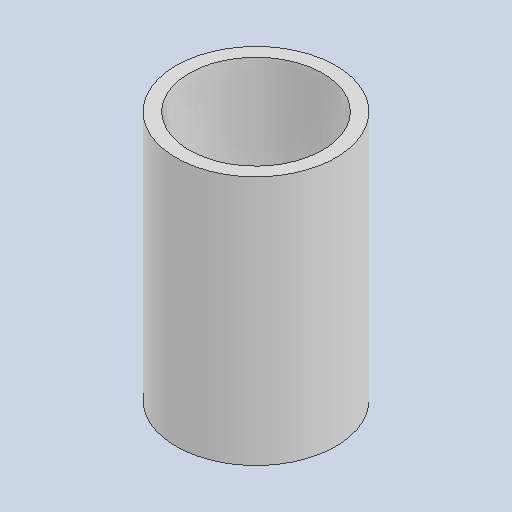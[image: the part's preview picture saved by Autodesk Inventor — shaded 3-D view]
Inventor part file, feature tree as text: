
AUTODESK INVENTOR PART (.ipt)
format: ipt  version: 2025.2 (Build 292293000, 293)  size: 88,576 bytes
history: native  units: in
note: dims shown in document units (in); Inventor stores cm internally (conversion verified against a paired STEP export)
features: other x3, sketch x1
ambient origin geometry x8: Origin, YZ Plane, XZ Plane, XY Plane, X Axis, Y Axis, Z Axis, Center Point
bodies: Solid1 (feature_tree)
feature tree (4):
  other  "Thin_spacer_custom.ipt"
  other  "Solid1::Thin_spacer_custom.ipt"
  other  "TaggingFeature1"
  sketch  "Sketch1"  dims[d0=0.3937in]
